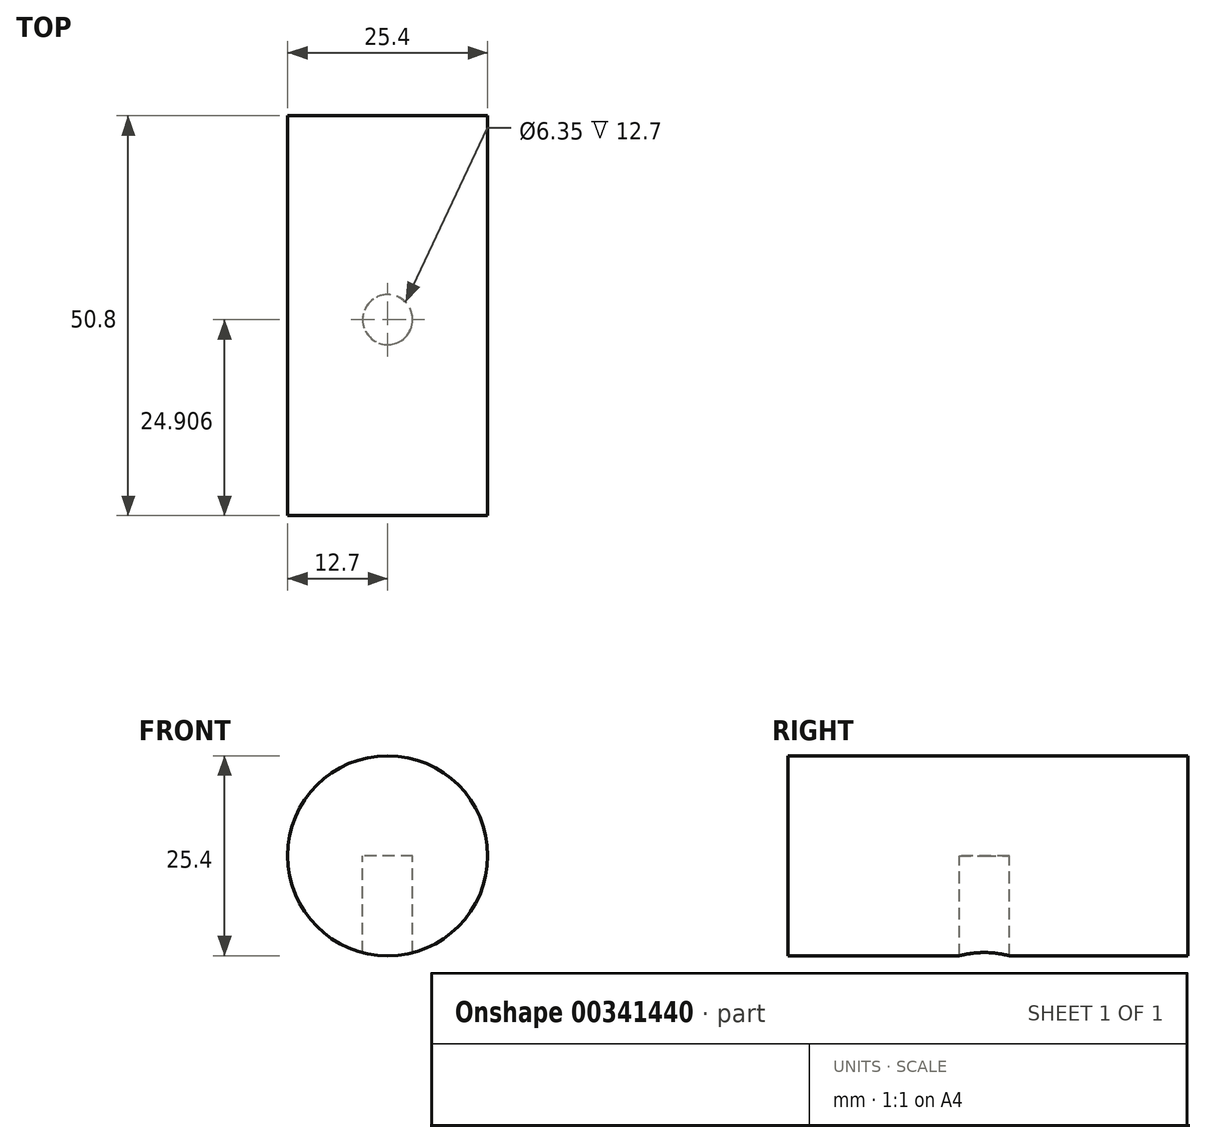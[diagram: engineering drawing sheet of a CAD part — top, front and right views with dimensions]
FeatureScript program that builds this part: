
annotation { "Feature Type Name" : "Feature", "Feature Type Description" : "" }
export const myFeature = defineFeature(function(context is Context, id is Id, definition is map)
    precondition{}
    {
        {
            var Q0;
            Q0=qCreatedBy(makeId("Front.planeOp"),FACE);
            var sketch = newSketch(context, id + "F0", { "sketchPlane" : qUnion([Q0])});
            skCircle(sketch, "E0", {"center": v(0, 0) * mm, "radius": 12.7 * mm});
            skSolve(sketch);
        }
        {
            var Q0;
            Q0=makeQuery(id+"F0.imprint","IMPRINT",FACE,{"disambiguationData":[TD([[makeQuery(id+"F0.imprint","IMPRINT",EDGE,{"derivedFrom":sQuery(id+"F0.wireOp",EDGE,"E0")}),1.0]])]});
            extrude(context, id + "F1", {"entities" : qUnion([Q0]), "depth" : 50.8 * mm});
        }
        {
            var Q0;
            Q0=qCreatedBy(makeId("Top.planeOp"),FACE);
            var sketch = newSketch(context, id + "F2", { "sketchPlane" : qUnion([Q0])});
            skCircle(sketch, "E1", {"center": v(0, -25.9) * mm, "radius": 3.18 * mm});
            skSolve(sketch);
        }
        {
            var Q0;
            Q0 = qSketchRegion(id + "F2", true);
            extrude(context, id + "F3", {"entities" : qUnion([Q0]), "operationType" : NewBodyOperationType.REMOVE, "oppositeDirection" : true, "depth" : 25.4 * mm});
        }
    });
